# Revit family: Zumtobel TECTON 2 motion sensors
name_source: partatom
category: Lighting Devices
units: mm (PartAtom-declared; Revit-internal decimal feet)

## family parameters
Cut with Voids When Loaded = No
Host = Face
Maintain Annotation Orientation = No
Part Type = Normal
Room Calculation Point = Yes
Round Connector Dimension = Use Diameter
Shared = Yes

## types (5) — shared parameters
Assembly Code = Pr_75_75_27_23
Description = Lighting and occupancy sensors
Export Type to IFC As = IfcSensorType
Luminaire Height = 90 mm
Luminaire Length = 250 mm
Luminaire Width = 60 mm
Manufacturer = Zumtobel Lighting
Type IFC Predefined Type = MOVEMENTSENSOR
zero-valued in all types: Default Elevation

## per-type parameters (varying)
| type | IS DALI Type | Material Housing | Model | Type Image | URL |
| PST PIR CF TEC2 WH | No | Zumtobel-Plastic-RAL 9003-Signal White | 22172954 | ZS_TE2_F_PST_Seite_WH.jpg | www.zumtobel.com/22172954 |
| PST PIR CF TEC2 BK | No | Zumtobel-Plastic-RAL 9005-Jet Black | 22173122 | ZS_TE2_F_PST_Seite_BK.jpg | www.zumtobel.com/22173122 |
| PST PIR S TEC2 BK | No | Zumtobel-Plastic-RAL 9005-Jet Black | 22173124 | ZS_TE2_F_PST_Seite_BK.jpg | www.zumtobel.com/22173124 |
| PST PIR S TEC2 WH | No | Zumtobel-Plastic-RAL 9003-Signal White | 22172955 | ZS_TE2_F_PST_Seite_WH.jpg | www.zumtobel.com/22172955 |
| PST PIR DALI-2 TEC2 WH | Yes | Zumtobel-Plastic-RAL 9003-Signal White | 22172960 | ZS_TE2_F_PST_Seite_WH.jpg | www.zumtobel.com/22172960 |

## geometry (parser evidence)
native form markers: Sweep x2
no freeform markers — native parametric forms only
